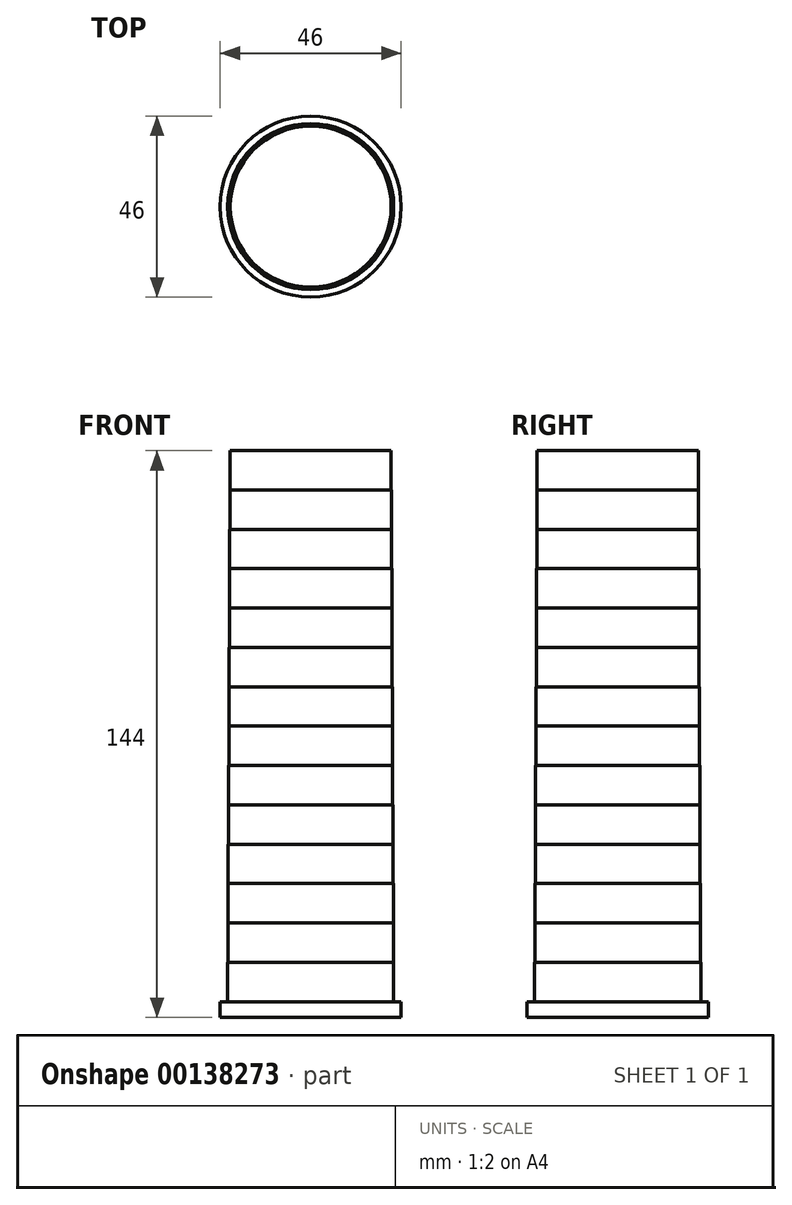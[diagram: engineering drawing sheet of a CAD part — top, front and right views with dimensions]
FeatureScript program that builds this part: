
annotation { "Feature Type Name" : "Feature", "Feature Type Description" : "" }
export const myFeature = defineFeature(function(context is Context, id is Id, definition is map)
    precondition{}
    {
        {
            var Q0;
            Q0=qCreatedBy(makeId("Top.planeOp"),FACE);
            var sketch = newSketch(context, id + "F0", { "sketchPlane" : qUnion([Q0])});
            skCircle(sketch, "E0", {"center": v(0, 0) * mm, "radius": 21.1 * mm});
            skSolve(sketch);
        }
        {
            var Q0;
            Q0=makeQuery(id+"F0.imprint","IMPRINT",FACE,{"disambiguationData":[TD([[makeQuery(id+"F0.imprint","IMPRINT",EDGE,{"derivedFrom":sQuery(id+"F0.wireOp",EDGE,"E0")}),1.0]])]});
            extrude(context, id + "F1", {"entities" : qUnion([Q0]), "depth" : 10 * mm});
        }
        {
            var Q0;
            Q0=makeQuery(id+"F1.opExtrude","CAP_FACE",FACE,{"disambiguationData":[OSD([sQuery(id+"F0.wireOp",EDGE,"E0")])],"isStart":false});
            var sketch = newSketch(context, id + "F2", { "sketchPlane" : qUnion([Q0])});
            skCircle(sketch, "E1", {"center": v(0, 0) * mm, "radius": 21.05 * mm});
            skSolve(sketch);
        }
        {
            var Q0;
            Q0 = qSketchRegion(id + "F2", true);
            extrude(context, id + "F3", {"entities" : qUnion([Q0]), "operationType" : NewBodyOperationType.ADD, "depth" : 10 * mm});
        }
        {
            var Q0;
            Q0=makeQuery(id+"F3.opExtrude","CAP_FACE",FACE,{"disambiguationData":[OSD([sQuery(id+"F2.wireOp",EDGE,"E1")])],"isStart":false});
            var sketch = newSketch(context, id + "F4", { "sketchPlane" : qUnion([Q0])});
            skCircle(sketch, "E2", {"center": v(0, 0) * mm, "radius": 21 * mm});
            skSolve(sketch);
        }
        {
            var Q0;
            Q0 = qSketchRegion(id + "F4", true);
            extrude(context, id + "F5", {"entities" : qUnion([Q0]), "operationType" : NewBodyOperationType.ADD, "depth" : 10 * mm});
        }
        {
            var Q0;
            Q0=makeQuery(id+"F5.opExtrude","CAP_FACE",FACE,{"disambiguationData":[OSD([sQuery(id+"F4.wireOp",EDGE,"E2")])],"isStart":false});
            var sketch = newSketch(context, id + "F6", { "sketchPlane" : qUnion([Q0])});
            skCircle(sketch, "E3", {"center": v(0, 0) * mm, "radius": 20.95 * mm});
            skSolve(sketch);
        }
        {
            var Q0;
            Q0 = qSketchRegion(id + "F6", true);
            extrude(context, id + "F7", {"entities" : qUnion([Q0]), "operationType" : NewBodyOperationType.ADD, "depth" : 10 * mm});
        }
        {
            var Q0;
            Q0=makeQuery(id+"F1.opExtrude","CAP_FACE",FACE,{"disambiguationData":[OSD([sQuery(id+"F0.wireOp",EDGE,"E0")])],"isStart":true});
            var sketch = newSketch(context, id + "F8", { "sketchPlane" : qUnion([Q0])});
            skCircle(sketch, "E4", {"center": v(0, 0) * mm, "radius": 23 * mm});
            skSolve(sketch);
        }
        {
            var Q0;
            Q0=makeQuery(id+"F8.imprint","IMPRINT",FACE,{"disambiguationData":[TD([[makeQuery(id+"F8.imprint","IMPRINT",EDGE,{"derivedFrom":sQuery(id+"F8.wireOp",EDGE,"E4")}),1.0]])]});
            var Q1;
            Q1=makeQuery(id+"F8.imprint","IMPRINT",FACE,{"disambiguationData":[TD([[makeQuery(id+"F8.imprint","IMPRINT",EDGE,{"derivedFrom":makeQuery(id+"F1.opExtrude","CAP_EDGE",EDGE,{"disambiguationData":[OSD([sQuery(id+"F0.wireOp",EDGE,"E0")])],"isStart":true})}),-1.0]])]});
            extrude(context, id + "F9", {"entities" : qUnion([Q0, Q1]), "operationType" : NewBodyOperationType.ADD, "depth" : 4 * mm});
        }
        {
            var Q0;
            Q0=makeQuery(id+"F7.opExtrude","CAP_FACE",FACE,{"disambiguationData":[OSD([sQuery(id+"F6.wireOp",EDGE,"E3")])],"isStart":false});
            var sketch = newSketch(context, id + "F10", { "sketchPlane" : qUnion([Q0])});
            skCircle(sketch, "E5", {"center": v(0, 0) * mm, "radius": 20.9 * mm});
            skSolve(sketch);
        }
        {
            var Q0;
            Q0 = qSketchRegion(id + "F10", true);
            extrude(context, id + "F11", {"entities" : qUnion([Q0]), "operationType" : NewBodyOperationType.ADD, "depth" : 10 * mm});
        }
        {
            var Q0;
            Q0=makeQuery(id+"F11.opExtrude","CAP_FACE",FACE,{"disambiguationData":[OSD([sQuery(id+"F10.wireOp",EDGE,"E5")])],"isStart":false});
            var sketch = newSketch(context, id + "F12", { "sketchPlane" : qUnion([Q0])});
            skCircle(sketch, "E6", {"center": v(0, 0) * mm, "radius": 20.85 * mm});
            skSolve(sketch);
        }
        {
            var Q0;
            Q0 = qSketchRegion(id + "F12", true);
            extrude(context, id + "F13", {"entities" : qUnion([Q0]), "operationType" : NewBodyOperationType.ADD, "depth" : 10 * mm});
        }
        {
            var Q0;
            Q0=makeQuery(id+"F13.opExtrude","CAP_FACE",FACE,{"disambiguationData":[OSD([sQuery(id+"F12.wireOp",EDGE,"E6")])],"isStart":false});
            var sketch = newSketch(context, id + "F14", { "sketchPlane" : qUnion([Q0])});
            skCircle(sketch, "E7", {"center": v(0, 0) * mm, "radius": 20.8 * mm});
            skSolve(sketch);
        }
        {
            var Q0;
            Q0 = qSketchRegion(id + "F14", true);
            extrude(context, id + "F15", {"entities" : qUnion([Q0]), "operationType" : NewBodyOperationType.ADD, "depth" : 10 * mm});
        }
        {
            var Q0;
            Q0=makeQuery(id+"F15.opExtrude","CAP_FACE",FACE,{"disambiguationData":[OSD([sQuery(id+"F14.wireOp",EDGE,"E7")])],"isStart":false});
            var sketch = newSketch(context, id + "F16", { "sketchPlane" : qUnion([Q0])});
            skCircle(sketch, "E8", {"center": v(0, 0) * mm, "radius": 20.75 * mm});
            skSolve(sketch);
        }
        {
            var Q0;
            Q0 = qSketchRegion(id + "F16", true);
            extrude(context, id + "F17", {"entities" : qUnion([Q0]), "operationType" : NewBodyOperationType.ADD, "depth" : 10 * mm});
        }
        {
            var Q0;
            Q0=makeQuery(id+"F17.opExtrude","CAP_FACE",FACE,{"disambiguationData":[OSD([sQuery(id+"F16.wireOp",EDGE,"E8")])],"isStart":false});
            var sketch = newSketch(context, id + "F18", { "sketchPlane" : qUnion([Q0])});
            skCircle(sketch, "E9", {"center": v(0, 0) * mm, "radius": 20.7 * mm});
            skSolve(sketch);
        }
        {
            var Q0;
            Q0 = qSketchRegion(id + "F18", true);
            extrude(context, id + "F19", {"entities" : qUnion([Q0]), "operationType" : NewBodyOperationType.ADD, "depth" : 10 * mm});
        }
        {
            var Q0;
            Q0=makeQuery(id+"F19.opExtrude","CAP_FACE",FACE,{"disambiguationData":[OSD([sQuery(id+"F18.wireOp",EDGE,"E9")])],"isStart":false});
            var sketch = newSketch(context, id + "F20", { "sketchPlane" : qUnion([Q0])});
            skCircle(sketch, "E10", {"center": v(0, 0) * mm, "radius": 20.65 * mm});
            skSolve(sketch);
        }
        {
            var Q0;
            Q0 = qSketchRegion(id + "F20", true);
            extrude(context, id + "F21", {"entities" : qUnion([Q0]), "operationType" : NewBodyOperationType.ADD, "depth" : 10 * mm});
        }
        {
            var Q0;
            Q0=makeQuery(id+"F21.opExtrude","CAP_FACE",FACE,{"disambiguationData":[OSD([sQuery(id+"F20.wireOp",EDGE,"E10")])],"isStart":false});
            var sketch = newSketch(context, id + "F22", { "sketchPlane" : qUnion([Q0])});
            skCircle(sketch, "E11", {"center": v(0, 0) * mm, "radius": 20.6 * mm});
            skSolve(sketch);
        }
        {
            var Q0;
            Q0 = qSketchRegion(id + "F22", true);
            extrude(context, id + "F23", {"entities" : qUnion([Q0]), "operationType" : NewBodyOperationType.ADD, "depth" : 10 * mm});
        }
        {
            var Q0;
            Q0=makeQuery(id+"F23.opExtrude","CAP_FACE",FACE,{"disambiguationData":[OSD([sQuery(id+"F22.wireOp",EDGE,"E11")])],"isStart":false});
            var sketch = newSketch(context, id + "F24", { "sketchPlane" : qUnion([Q0])});
            skCircle(sketch, "E12", {"center": v(0, 0) * mm, "radius": 20.55 * mm});
            skSolve(sketch);
        }
        {
            var Q0;
            Q0 = qSketchRegion(id + "F24", true);
            extrude(context, id + "F25", {"entities" : qUnion([Q0]), "operationType" : NewBodyOperationType.ADD, "depth" : 10 * mm});
        }
        {
            var Q0;
            Q0=makeQuery(id+"F25.opExtrude","CAP_FACE",FACE,{"disambiguationData":[OSD([sQuery(id+"F24.wireOp",EDGE,"E12")])],"isStart":false});
            var sketch = newSketch(context, id + "F26", { "sketchPlane" : qUnion([Q0])});
            skCircle(sketch, "E13", {"center": v(0, 0) * mm, "radius": 20.5 * mm});
            skSolve(sketch);
        }
        {
            var Q0;
            Q0 = qSketchRegion(id + "F26", true);
            extrude(context, id + "F27", {"entities" : qUnion([Q0]), "operationType" : NewBodyOperationType.ADD, "depth" : 10 * mm});
        }
        {
            var Q0;
            Q0=makeQuery(id+"F27.opExtrude","CAP_FACE",FACE,{"disambiguationData":[OSD([sQuery(id+"F26.wireOp",EDGE,"E13")])],"isStart":false});
            var sketch = newSketch(context, id + "F28", { "sketchPlane" : qUnion([Q0])});
            skCircle(sketch, "E14", {"center": v(0, 0) * mm, "radius": 20.45 * mm});
            skSolve(sketch);
        }
        {
            var Q0;
            Q0 = qSketchRegion(id + "F28", true);
            extrude(context, id + "F29", {"entities" : qUnion([Q0]), "operationType" : NewBodyOperationType.ADD, "depth" : 10 * mm});
        }
    });
